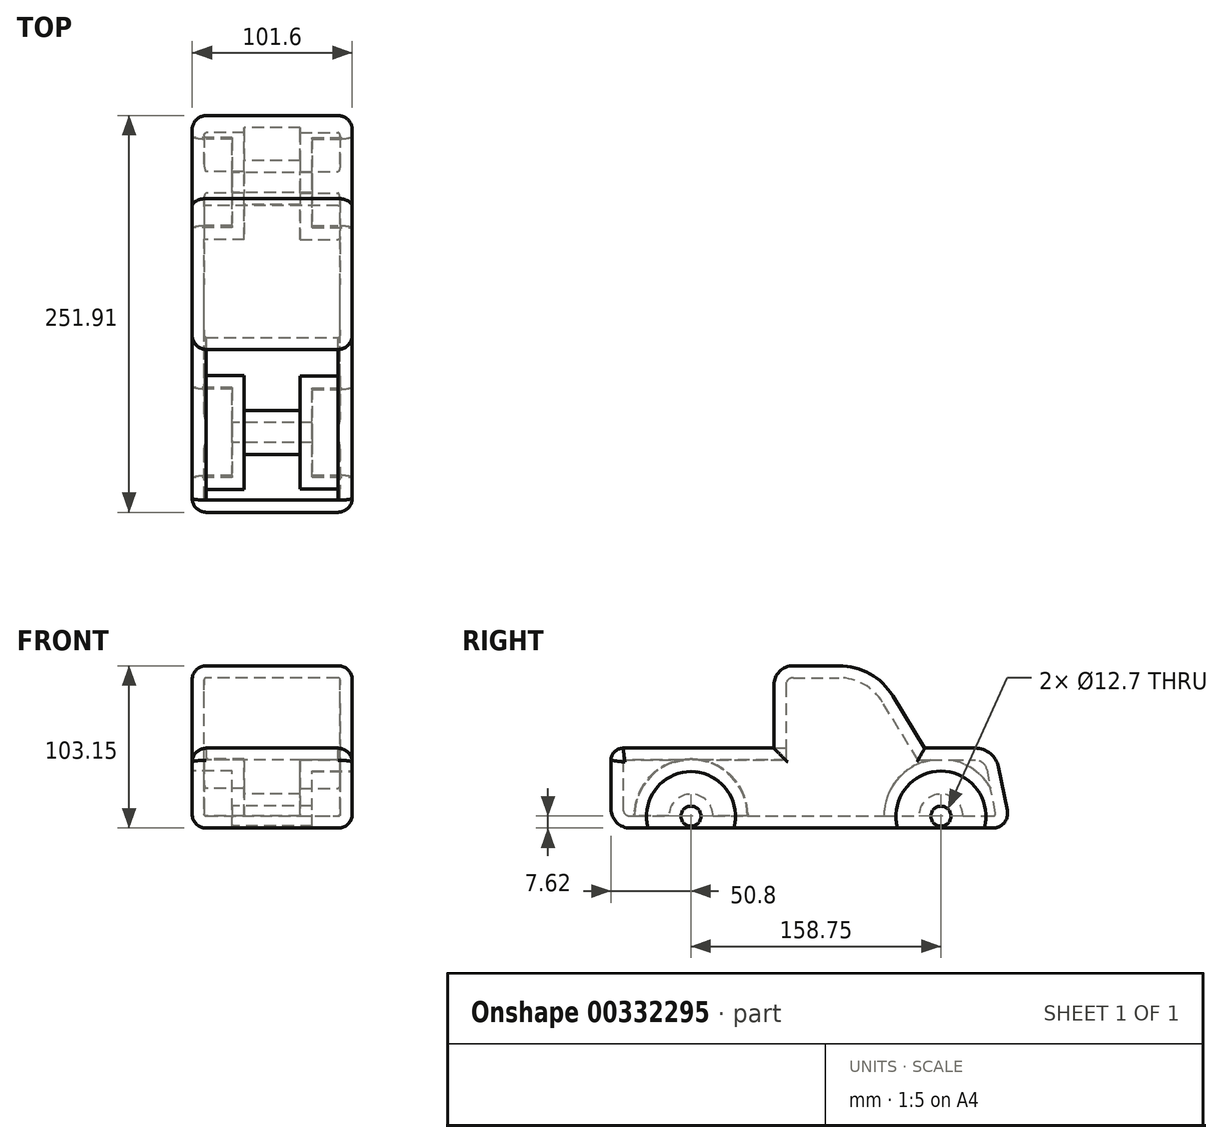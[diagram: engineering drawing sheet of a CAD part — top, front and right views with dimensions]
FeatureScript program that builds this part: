
annotation { "Feature Type Name" : "Feature", "Feature Type Description" : "" }
export const myFeature = defineFeature(function(context is Context, id is Id, definition is map)
    precondition{}
    {
        {
            var Q0;
            Q0=qCreatedBy(makeId("Right.planeOp"),FACE);
            var sketch = newSketch(context, id + "F0", { "sketchPlane" : qUnion([Q0])});
            skLineSegment(sketch, "E0.bottom", {"start": v(12.28, 0) * mm, "end": v(242.5, 0) * mm});
            skLineSegment(sketch, "E0.top", {"start": v(7.7, 50.8) * mm, "end": v(103.46, 50.8) * mm});
            skLineSegment(sketch, "E0.left", {"start": v(0, 12.28) * mm, "end": v(0, 43.1) * mm});
            skLineSegment(sketch, "E1.top", {"start": v(144.78, 103.15) * mm, "end": v(115.74, 103.15) * mm});
            skLineSegment(sketch, "E1.right", {"start": v(103.46, 50.8) * mm, "end": v(103.46, 90.86) * mm});
            skLineSegment(sketch, "E2", {"start": v(179.04, 83.9) * mm, "end": v(199.23, 50.8) * mm});
            skLineSegment(sketch, "E3", {"start": v(251.72, 11.28) * mm, "end": v(246.16, 38.78) * mm});
            skArc(sketch, "E4.filletArc", {"start": v(246.16, 38.78) * mm, "mid": v(240.96, 47.41) * mm, "end": v(231.47, 50.8) * mm});
            skArc(sketch, "E5.filletArc", {"start": v(242.5, 0) * mm, "mid": v(249.78, 3.45) * mm, "end": v(251.72, 11.28) * mm});
            skArc(sketch, "E6.filletArc", {"start": v(179.04, 83.9) * mm, "mid": v(164.42, 98) * mm, "end": v(144.78, 103.15) * mm});
            skArc(sketch, "E7.filletArc", {"start": v(115.74, 103.15) * mm, "mid": v(107.06, 99.55) * mm, "end": v(103.46, 90.86) * mm});
            skLineSegment(sketch, "E8.trimOffspring", {"start": v(199.23, 50.8) * mm, "end": v(231.47, 50.8) * mm});
            skPoint(sketch, "E9.visualSharp", {"position": v(0, 0) * mm});
            skArc(sketch, "E9.filletArc", {"start": v(0, 12.28) * mm, "mid": v(3.6, 3.6) * mm, "end": v(12.28, 0) * mm});
            skArc(sketch, "E10.filletArc", {"start": v(7.7, 50.8) * mm, "mid": v(2.26, 48.54) * mm, "end": v(0, 43.1) * mm});
            skSolve(sketch);
        }
        {
            var Q0;
            Q0=makeQuery(id+"F0.imprint","IMPRINT",FACE,{"disambiguationData":[TD([[makeQuery(id+"F0.imprint","IMPRINT",EDGE,{"derivedFrom":sQuery(id+"F0.wireOp",EDGE,"E0.bottom")}),1.0]])]});
            extrude(context, id + "F1", {"entities" : qUnion([Q0]), "depth" : 101.6 * mm});
        }
        {
            var Q0;
            Q0=makeQuery(id+"F1.opExtrude","CAP_FACE",FACE,{"disambiguationData":[OSD([sQuery(id+"F0.wireOp",EDGE,"E0.bottom"),sQuery(id+"F0.wireOp",EDGE,"E0.top"),sQuery(id+"F0.wireOp",EDGE,"E0.left"),sQuery(id+"F0.wireOp",EDGE,"E1.top"),sQuery(id+"F0.wireOp",EDGE,"E1.right"),sQuery(id+"F0.wireOp",EDGE,"E2"),sQuery(id+"F0.wireOp",EDGE,"E3"),sQuery(id+"F0.wireOp",EDGE,"E4.filletArc"),sQuery(id+"F0.wireOp",EDGE,"E5.filletArc"),sQuery(id+"F0.wireOp",EDGE,"E6.filletArc"),sQuery(id+"F0.wireOp",EDGE,"E7.filletArc"),sQuery(id+"F0.wireOp",EDGE,"E8.trimOffspring"),sQuery(id+"F0.wireOp",EDGE,"E9.filletArc"),sQuery(id+"F0.wireOp",EDGE,"E10.filletArc")])],"isStart":false});
            var sketch = newSketch(context, id + "F2", { "sketchPlane" : qUnion([Q0])});
            skLineSegment(sketch, "E11", {"start": v(0, 0) * mm, "end": v(0, 7.62) * mm, "construction": true});
            skLineSegment(sketch, "E12", {"start": v(0, 7.62) * mm, "end": v(50.8, 7.62) * mm, "construction": true});
            skLineSegment(sketch, "E13", {"start": v(50.8, 7.62) * mm, "end": v(209.55, 7.62) * mm, "construction": true});
            skCircle(sketch, "E14", {"center": v(50.8, 7.62) * mm, "radius": 28.26 * mm});
            skCircle(sketch, "E15", {"center": v(209.55, 7.62) * mm, "radius": 28.58 * mm});
            skSolve(sketch);
        }
        {
            var Q0;
            Q0=qSketchRegion(id+"F2",true);
            extrude(context, id + "F3", {"entities" : qUnion([Q0]), "operationType" : NewBodyOperationType.REMOVE, "oppositeDirection" : true, "depth" : 25.4 * mm});
        }
        {
            var Q0;
            Q0=makeQuery(id+"F1.opExtrude","CAP_FACE",FACE,{"disambiguationData":[OSD([sQuery(id+"F0.wireOp",EDGE,"E0.bottom"),sQuery(id+"F0.wireOp",EDGE,"E0.top"),sQuery(id+"F0.wireOp",EDGE,"E0.left"),sQuery(id+"F0.wireOp",EDGE,"E1.top"),sQuery(id+"F0.wireOp",EDGE,"E1.right"),sQuery(id+"F0.wireOp",EDGE,"E2"),sQuery(id+"F0.wireOp",EDGE,"E3"),sQuery(id+"F0.wireOp",EDGE,"E4.filletArc"),sQuery(id+"F0.wireOp",EDGE,"E5.filletArc"),sQuery(id+"F0.wireOp",EDGE,"E6.filletArc"),sQuery(id+"F0.wireOp",EDGE,"E7.filletArc"),sQuery(id+"F0.wireOp",EDGE,"E8.trimOffspring"),sQuery(id+"F0.wireOp",EDGE,"E9.filletArc"),sQuery(id+"F0.wireOp",EDGE,"E10.filletArc")])],"isStart":true});
            var sketch = newSketch(context, id + "F4", { "sketchPlane" : qUnion([Q0])});
            skLineSegment(sketch, "E16", {"start": v(0, 0) * mm, "end": v(0, 7.62) * mm, "construction": true});
            skLineSegment(sketch, "E17", {"start": v(0, 7.62) * mm, "end": v(-50.8, 7.62) * mm, "construction": true});
            skLineSegment(sketch, "E18", {"start": v(-50.8, 7.62) * mm, "end": v(-209.55, 7.62) * mm, "construction": true});
            skCircle(sketch, "E19", {"center": v(-50.8, 7.62) * mm, "radius": 28.58 * mm});
            skCircle(sketch, "E20", {"center": v(-209.55, 7.62) * mm, "radius": 28.58 * mm});
            skSolve(sketch);
        }
        {
            var Q0;
            Q0=qSketchRegion(id+"F4",true);
            extrude(context, id + "F5", {"entities" : qUnion([Q0]), "operationType" : NewBodyOperationType.REMOVE, "oppositeDirection" : true, "depth" : 25.4 * mm});
        }
        {
            var Q0;
            Q0=makeQuery(id+"F5.boolean.opBoolean","COPY",FACE,{"derivedFrom":makeQuery(id+"F5.opExtrude","CAP_FACE",FACE,{"disambiguationData":[OSD([sQuery(id+"F4.wireOp",EDGE,"E20")])],"isStart":false})});
            var sketch = newSketch(context, id + "F6", { "sketchPlane" : qUnion([Q0])});
            skCircle(sketch, "E21", {"center": v(-209.55, 7.62) * mm, "radius": 6.35 * mm});
            skSolve(sketch);
        }
        {
            var Q0;
            Q0=makeQuery(id+"F6.imprint","IMPRINT",FACE,{"disambiguationData":[TD([[makeQuery(id+"F6.imprint","IMPRINT",EDGE,{"derivedFrom":sQuery(id+"F6.wireOp",EDGE,"E21")}),1.0]])]});
            extrude(context, id + "F7", {"entities" : qUnion([Q0]), "operationType" : NewBodyOperationType.REMOVE, "endBound" : BoundingType.UP_TO_NEXT, "oppositeDirection" : true, "depth" : 25.4 * mm});
        }
        {
            var Q0;
            Q0=makeQuery(id+"F5.boolean.opBoolean","COPY",FACE,{"derivedFrom":makeQuery(id+"F5.opExtrude","CAP_FACE",FACE,{"disambiguationData":[OSD([sQuery(id+"F4.wireOp",EDGE,"E19")])],"isStart":false})});
            var sketch = newSketch(context, id + "F8", { "sketchPlane" : qUnion([Q0])});
            skCircle(sketch, "E22", {"center": v(-50.8, 7.62) * mm, "radius": 6.35 * mm});
            skSolve(sketch);
        }
        {
            var Q0;
            Q0=makeQuery(id+"F8.imprint","IMPRINT",FACE,{"disambiguationData":[TD([[makeQuery(id+"F8.imprint","IMPRINT",EDGE,{"derivedFrom":sQuery(id+"F8.wireOp",EDGE,"E22")}),1.0]])]});
            extrude(context, id + "F9", {"entities" : qUnion([Q0]), "operationType" : NewBodyOperationType.REMOVE, "endBound" : BoundingType.UP_TO_NEXT, "oppositeDirection" : true, "depth" : 25.4 * mm});
        }
        {
            var Q0;
            Q0=makeQuery(id+"F1.opExtrude","CAP_EDGE",EDGE,{"disambiguationData":[OSD([sQuery(id+"F0.wireOp",EDGE,"E2")])],"isStart":true});
            var Q1;
            Q1=makeQuery(id+"F1.opExtrude","CAP_EDGE",EDGE,{"disambiguationData":[OSD([sQuery(id+"F0.wireOp",EDGE,"E8.trimOffspring")])],"isStart":true});
            var Q2;
            Q2=makeQuery(id+"F1.opExtrude","CAP_EDGE",EDGE,{"disambiguationData":[OSD([sQuery(id+"F0.wireOp",EDGE,"E0.top")])],"isStart":true});
            var Q3;
            {var subQ0=sQuery(id+"F0.wireOp",EDGE,"E0.bottom");Q3=makeQuery(id+"F5.boolean.opBoolean","SPLIT",EDGE,{"disambiguationData":[TD([makeQuery(id+"F1.opExtrude","SWEPT_FACE",FACE,{"disambiguationData":[OSD([subQ0])]}),makeQuery(id+"F1.opExtrude","CAP_FACE",FACE,{"disambiguationData":[OSD([subQ0,sQuery(id+"F0.wireOp",EDGE,"E0.top"),sQuery(id+"F0.wireOp",EDGE,"E0.left"),sQuery(id+"F0.wireOp",EDGE,"E1.top"),sQuery(id+"F0.wireOp",EDGE,"E1.right"),sQuery(id+"F0.wireOp",EDGE,"E2"),sQuery(id+"F0.wireOp",EDGE,"E3"),sQuery(id+"F0.wireOp",EDGE,"E4.filletArc"),sQuery(id+"F0.wireOp",EDGE,"E5.filletArc"),sQuery(id+"F0.wireOp",EDGE,"E6.filletArc"),sQuery(id+"F0.wireOp",EDGE,"E7.filletArc"),sQuery(id+"F0.wireOp",EDGE,"E8.trimOffspring"),sQuery(id+"F0.wireOp",EDGE,"E9.filletArc"),sQuery(id+"F0.wireOp",EDGE,"E10.filletArc")])],"isStart":true}),makeQuery(id+"F5.opExtrude","SWEPT_FACE",FACE,{"disambiguationData":[OSD([sQuery(id+"F4.wireOp",EDGE,"E19")])]}),makeQuery(id+"F5.opExtrude","SWEPT_FACE",FACE,{"disambiguationData":[OSD([sQuery(id+"F4.wireOp",EDGE,"E20")])]})])],"derivedFrom":makeQuery(id+"F1.opExtrude","CAP_EDGE",EDGE,{"disambiguationData":[OSD([subQ0])],"isStart":true})});}
            var Q4;
            Q4=makeQuery(id+"F1.opExtrude","CAP_EDGE",EDGE,{"disambiguationData":[OSD([sQuery(id+"F0.wireOp",EDGE,"E0.top")])],"isStart":false});
            var Q5;
            Q5=makeQuery(id+"F1.opExtrude","CAP_EDGE",EDGE,{"disambiguationData":[OSD([sQuery(id+"F0.wireOp",EDGE,"E1.right")])],"isStart":false});
            var Q6;
            Q6=makeQuery(id+"F1.opExtrude","CAP_EDGE",EDGE,{"disambiguationData":[OSD([sQuery(id+"F0.wireOp",EDGE,"E8.trimOffspring")])],"isStart":false});
            var Q7;
            {var subQ0=sQuery(id+"F0.wireOp",EDGE,"E0.bottom");Q7=makeQuery(id+"F3.boolean.opBoolean","SPLIT",EDGE,{"disambiguationData":[TD([makeQuery(id+"F1.opExtrude","SWEPT_FACE",FACE,{"disambiguationData":[OSD([subQ0])]}),makeQuery(id+"F1.opExtrude","CAP_FACE",FACE,{"disambiguationData":[OSD([subQ0,sQuery(id+"F0.wireOp",EDGE,"E0.top"),sQuery(id+"F0.wireOp",EDGE,"E0.left"),sQuery(id+"F0.wireOp",EDGE,"E1.top"),sQuery(id+"F0.wireOp",EDGE,"E1.right"),sQuery(id+"F0.wireOp",EDGE,"E2"),sQuery(id+"F0.wireOp",EDGE,"E3"),sQuery(id+"F0.wireOp",EDGE,"E4.filletArc"),sQuery(id+"F0.wireOp",EDGE,"E5.filletArc"),sQuery(id+"F0.wireOp",EDGE,"E6.filletArc"),sQuery(id+"F0.wireOp",EDGE,"E7.filletArc"),sQuery(id+"F0.wireOp",EDGE,"E8.trimOffspring"),sQuery(id+"F0.wireOp",EDGE,"E9.filletArc"),sQuery(id+"F0.wireOp",EDGE,"E10.filletArc")])],"isStart":false}),makeQuery(id+"F3.opExtrude","SWEPT_FACE",FACE,{"disambiguationData":[OSD([sQuery(id+"F2.wireOp",EDGE,"E14")])]}),makeQuery(id+"F3.opExtrude","SWEPT_FACE",FACE,{"disambiguationData":[OSD([sQuery(id+"F2.wireOp",EDGE,"E15")])]})])],"derivedFrom":makeQuery(id+"F1.opExtrude","CAP_EDGE",EDGE,{"disambiguationData":[OSD([subQ0])],"isStart":false})});}
            fillet(context, id + "F10", {"entities" : qUnion([Q0, Q1, Q2, Q3, Q4, Q5, Q6, Q7]), "radius" : 8.9 * mm, "tangentPropagation" : true, "allowEdgeOverflow" : false});
        }
        {
            var Q0;
            Q0=makeQuery(id+"F1.opExtrude","SWEPT_FACE",FACE,{"disambiguationData":[OSD([sQuery(id+"F0.wireOp",EDGE,"E0.top")])]});
            shell(context, id + "F11", {"entities" : qUnion([Q0]), "thickness" : 7.62 * mm});
        }
    });
